SOLIDWORKS PART (.sldprt)
format: sldprt  version: not decoded by parser v0  size: 1,182,720 bytes
history: native  units: mm
features: sketch x8, plane x3, extrude x3, sweep x2, material x1, helix x1, fillet x1, pattern_circular x1, cut_extrude x1 (+10 scaffold rows collapsed)
feature tree (31):
  scaffold x10  (default folders/planes/origin — collapsed)
  material  "Matériau <non spécifié>"
  plane  "Plan1"
  plane  "Plan2"
  plane  "Plan3"
  sketch  "Esquisse1"  dims[Dp=36.108mm]
  sketch  "Esquisse2"  dims[c1.Db=36.813mm c1.Dn=39.233mm c1.Dt=41.733mm c1.m=0.5mm c1.D2=7.0mm c1.ap=20.0deg c1.D1=~9.395278mm c2.D1=20.854deg c2.D2=~9.395278mm c3.D2=~24.138828deg c3.D1=8.0mm c3.Tn=~0.859437deg c4.D2=8.0mm c4.Tt=~2.463719deg c4.D3=9.5mm c4.Ts=~2.864789deg]
  extrude  "Base-Extrusion"  Depth=11mm
  sketch  "Esquisse3"  dims[D1=40.0mm]
  helix  "Hélice1"  Pitch=5.5mm
  sweep  "Boss.-Balayage1"
  sketch  "Esquisse5"  dims[D1=0.0mm]
  sketch  "Esquisse6"  dims[Hélice2=0.0 D3=5.5mm D4=778.195mm D5=~7.067637mm D7=0.0deg]
  sweep  "Boss.-Balayage2"
  fillet  "Congé1"  Radius=0.416mm
  pattern_circular  "Répétition circulaire2"  Count=31 Angle=360deg
  sketch  "Esquisse4"  dims[D1=17.0mm]
  cut_extrude  "Enlèv. mat.-Extru.2"  [1 undecoded]
  sketch  "Esquisse7"
  extrude  "Cylindre primitif"  [1 undecoded]
  sketch  "Esquisse8"
  extrude  "Enlèv. mat.-Extru.3"  [1 undecoded]
decode coverage: 10 of 17 modeling features carry decoded parameters
note: ~ marks probable driven/reference dimensions
note: 3 parameter values undecoded
summary: no parameter record found for 3 features
note: suppression state not decoded; provenance and decode notes live in map.json
